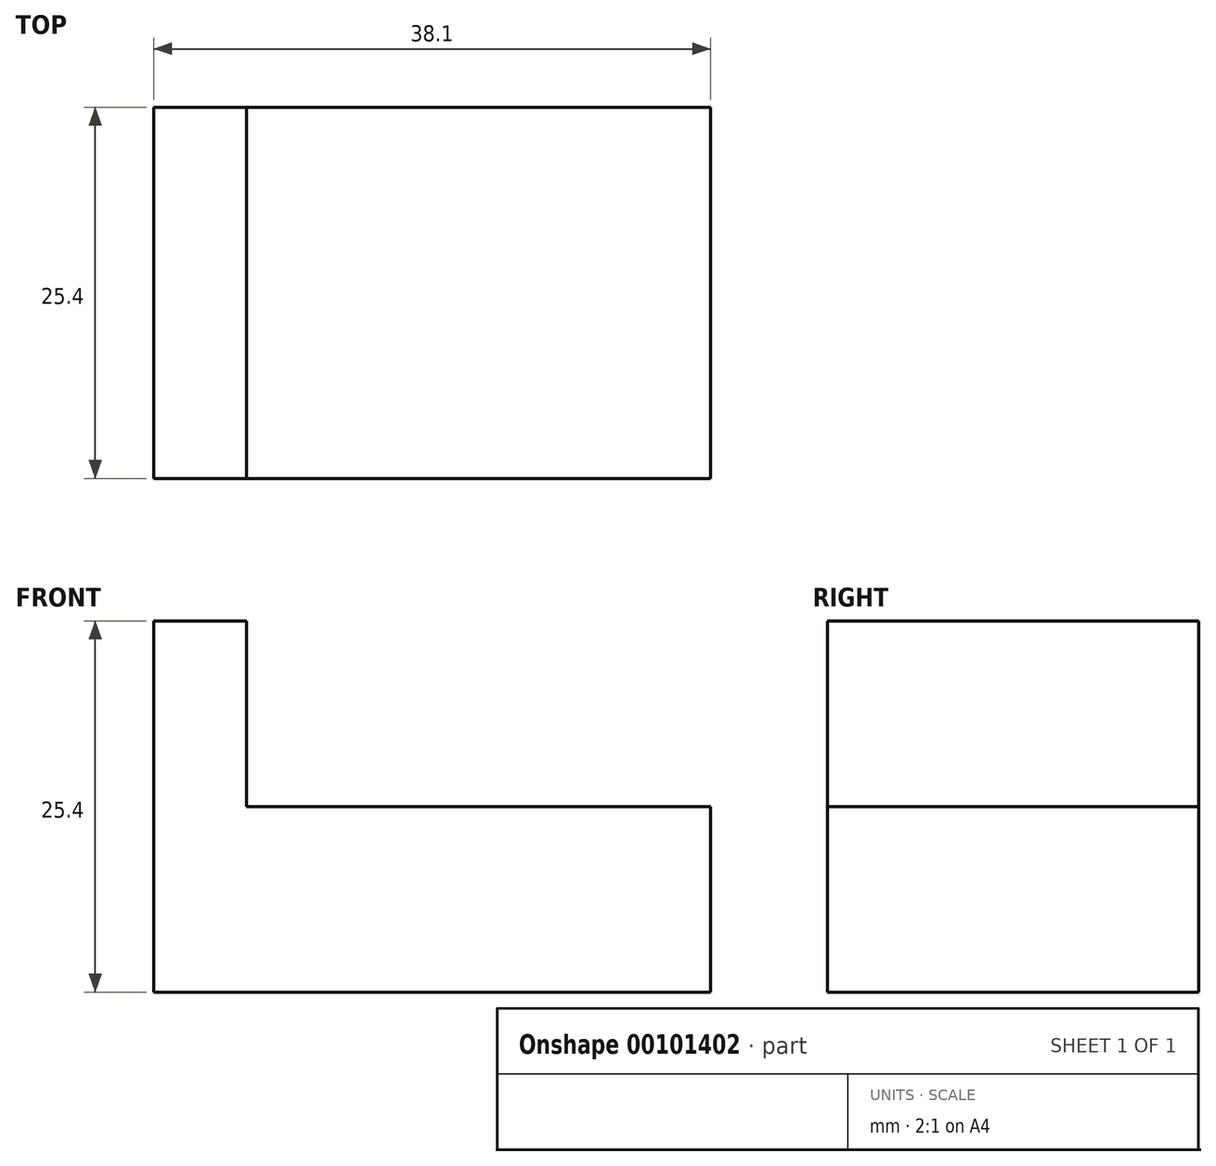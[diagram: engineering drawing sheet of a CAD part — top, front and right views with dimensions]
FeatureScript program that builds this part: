
annotation { "Feature Type Name" : "Feature", "Feature Type Description" : "" }
export const myFeature = defineFeature(function(context is Context, id is Id, definition is map)
    precondition{}
    {
        {
            var Q0;
            Q0=qCreatedBy(makeId("Front.planeOp"),FACE);
            var sketch = newSketch(context, id + "F0", { "sketchPlane" : qUnion([Q0])});
            skLineSegment(sketch, "E0", {"start": v(0, 0) * mm, "end": v(38.1, 0) * mm});
            skLineSegment(sketch, "E1", {"start": v(38.1, 0) * mm, "end": v(38.1, 12.7) * mm});
            skLineSegment(sketch, "E2", {"start": v(38.1, 12.7) * mm, "end": v(6.35, 12.7) * mm});
            skLineSegment(sketch, "E3", {"start": v(6.35, 12.7) * mm, "end": v(6.35, 25.4) * mm});
            skLineSegment(sketch, "E4", {"start": v(6.35, 25.4) * mm, "end": v(0, 25.4) * mm});
            skLineSegment(sketch, "E5", {"start": v(0, 25.4) * mm, "end": v(0, 0) * mm});
            skSolve(sketch);
        }
        {
            var Q0;
            Q0=makeQuery(id+"F0.imprint","IMPRINT",FACE,{"disambiguationData":[TD([[makeQuery(id+"F0.imprint","IMPRINT",EDGE,{"derivedFrom":sQuery(id+"F0.wireOp",EDGE,"E0")}),1.0]])]});
            var Q1;
            Q1=sQuery(id+"F0.wireOp",EDGE,"E4");
            var Q2;
            Q2=sQuery(id+"F0.wireOp",EDGE,"E0");
            var Q3;
            Q3=sQuery(id+"F0.wireOp",EDGE,"E3");
            var Q4;
            Q4=sQuery(id+"F0.wireOp",EDGE,"E5");
            var Q5;
            Q5=sQuery(id+"F0.wireOp",EDGE,"E1");
            var Q6;
            Q6=sQuery(id+"F0.wireOp",EDGE,"E2");
            extrude(context, id + "F1", {"entities" : qUnion([Q0]), "surfaceEntities" : qUnion([Q1, Q2, Q3, Q4, Q5, Q6]), "depth" : 25.4 * mm});
        }
    });
